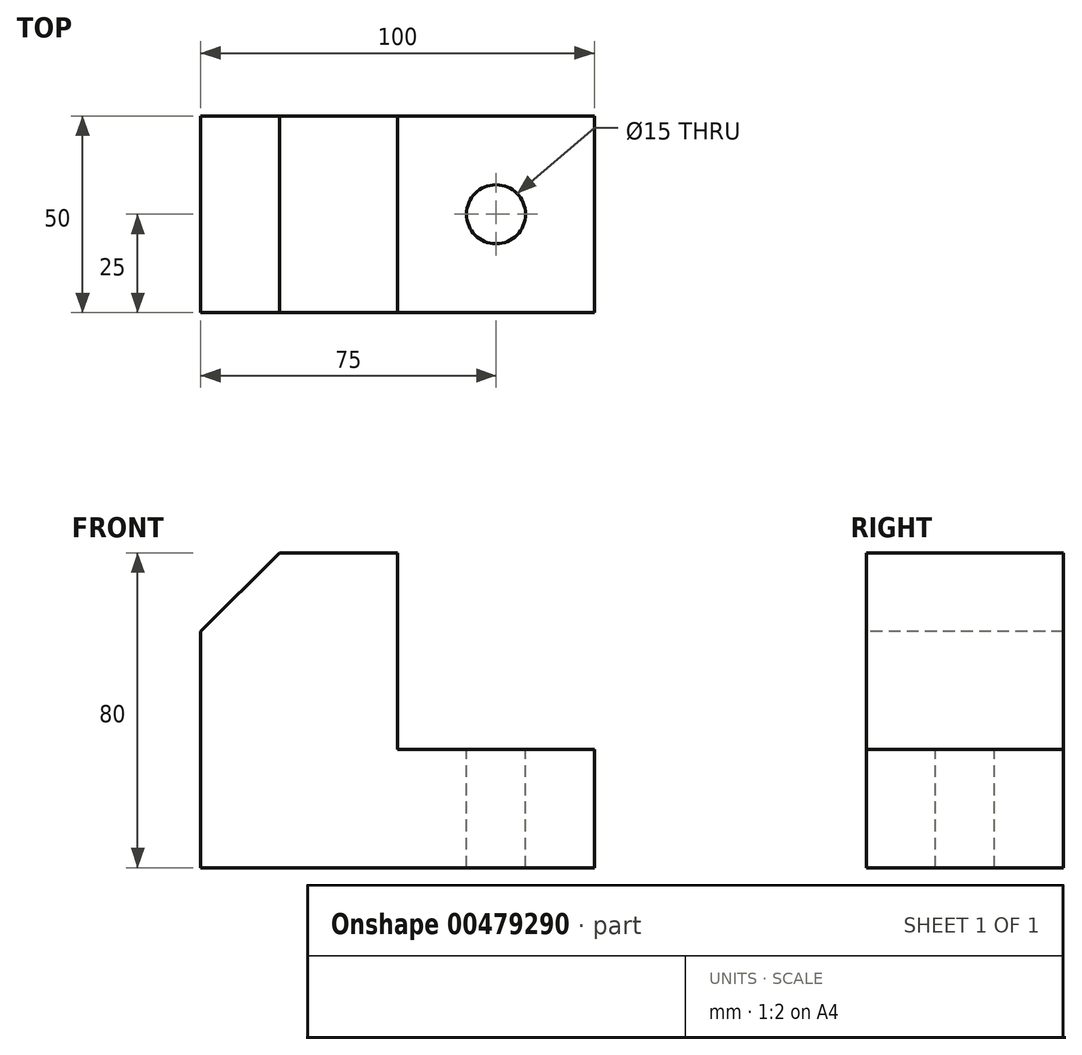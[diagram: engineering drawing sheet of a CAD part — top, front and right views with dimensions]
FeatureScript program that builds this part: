
annotation { "Feature Type Name" : "Feature", "Feature Type Description" : "" }
export const myFeature = defineFeature(function(context is Context, id is Id, definition is map)
    precondition{}
    {
        {
            var Q0;
            Q0=qCreatedBy(makeId("Top.planeOp"),FACE);
            var sketch = newSketch(context, id + "F0", { "sketchPlane" : qUnion([Q0])});
            skLineSegment(sketch, "E0.bottom", {"start": v(0, 0) * mm, "end": v(100, 0) * mm});
            skLineSegment(sketch, "E0.top", {"start": v(0, 50) * mm, "end": v(100, 50) * mm});
            skLineSegment(sketch, "E0.left", {"start": v(0, 0) * mm, "end": v(0, 50) * mm});
            skLineSegment(sketch, "E0.right", {"start": v(100, 0) * mm, "end": v(100, 50) * mm});
            skSolve(sketch);
        }
        {
            var Q0;
            Q0 = qSketchRegion(id + "F0", true);
            extrude(context, id + "F1", {"entities" : qUnion([Q0]), "depth" : 30 * mm});
        }
        {
            var Q0;
            Q0=makeQuery(id+"F1.opExtrude","CAP_FACE",FACE,{"disambiguationData":[OSD([sQuery(id+"F0.wireOp",EDGE,"E0.bottom"),sQuery(id+"F0.wireOp",EDGE,"E0.top"),sQuery(id+"F0.wireOp",EDGE,"E0.left"),sQuery(id+"F0.wireOp",EDGE,"E0.right")])],"isStart":false});
            var sketch = newSketch(context, id + "F2", { "sketchPlane" : qUnion([Q0])});
            skLineSegment(sketch, "E1.bottom", {"start": v(0, 50) * mm, "end": v(50, 50) * mm});
            skLineSegment(sketch, "E1.top", {"start": v(0, 0) * mm, "end": v(50, 0) * mm});
            skLineSegment(sketch, "E1.left", {"start": v(0, 50) * mm, "end": v(0, 0) * mm});
            skLineSegment(sketch, "E1.right", {"start": v(50, 50) * mm, "end": v(50, 0) * mm});
            skSolve(sketch);
        }
        {
            var Q0;
            Q0 = qSketchRegion(id + "F2", true);
            extrude(context, id + "F3", {"entities" : qUnion([Q0]), "operationType" : NewBodyOperationType.ADD, "depth" : 50 * mm});
        }
        {
            var Q0;
            Q0=makeQuery(id+"F1.opExtrude","CAP_FACE",FACE,{"disambiguationData":[OSD([sQuery(id+"F0.wireOp",EDGE,"E0.bottom"),sQuery(id+"F0.wireOp",EDGE,"E0.top"),sQuery(id+"F0.wireOp",EDGE,"E0.left"),sQuery(id+"F0.wireOp",EDGE,"E0.right")])],"isStart":false});
            var sketch = newSketch(context, id + "F4", { "sketchPlane" : qUnion([Q0])});
            skLineSegment(sketch, "E2", {"start": v(50, 50) * mm, "end": v(100, 0) * mm});
            skLineSegment(sketch, "E3", {"start": v(50, 0) * mm, "end": v(100, 50) * mm});
            skCircle(sketch, "E4", {"center": v(75, 25) * mm, "radius": 7.5 * mm});
            skSolve(sketch);
        }
        {
            var Q0;
            Q0 = qSketchRegion(id + "F4", true);
            extrude(context, id + "F5", {"entities" : qUnion([Q0]), "operationType" : NewBodyOperationType.REMOVE, "endBound" : BoundingType.THROUGH_ALL, "oppositeDirection" : true, "depth" : 25 * mm});
        }
        {
            var Q0;
            Q0=makeQuery(id+"F3.boolean.opBoolean","MERGE",FACE,{"derivedFrom":[makeQuery(id+"F1.opExtrude","SWEPT_FACE",FACE,{"disambiguationData":[OSD([sQuery(id+"F0.wireOp",EDGE,"E0.bottom")])]}),makeQuery(id+"F3.opExtrude","SWEPT_FACE",FACE,{"disambiguationData":[OSD([sQuery(id+"F2.wireOp",EDGE,"E1.top")])]})]});
            var sketch = newSketch(context, id + "F6", { "sketchPlane" : qUnion([Q0])});
            skLineSegment(sketch, "E5", {"start": v(0, 60) * mm, "end": v(20, 80) * mm});
            skSolve(sketch);
        }
        {
            var Q0;
            Q0 = qSketchRegion(id + "F6", true);
            var Q1;
            {var subQ0=sQuery(id+"F6.wireOp",EDGE,"E5");Q1=makeQuery(id+"F6.imprint","IMPRINT",FACE,{"disambiguationData":[TD([[makeQuery(id+"F6.imprint","IMPRINT",EDGE,{"derivedFrom":subQ0}),1.0]])]});}
            extrude(context, id + "F7", {"entities" : qUnion([Q0, Q1]), "operationType" : NewBodyOperationType.REMOVE, "endBound" : BoundingType.THROUGH_ALL, "oppositeDirection" : true, "depth" : 25 * mm});
        }
    });
